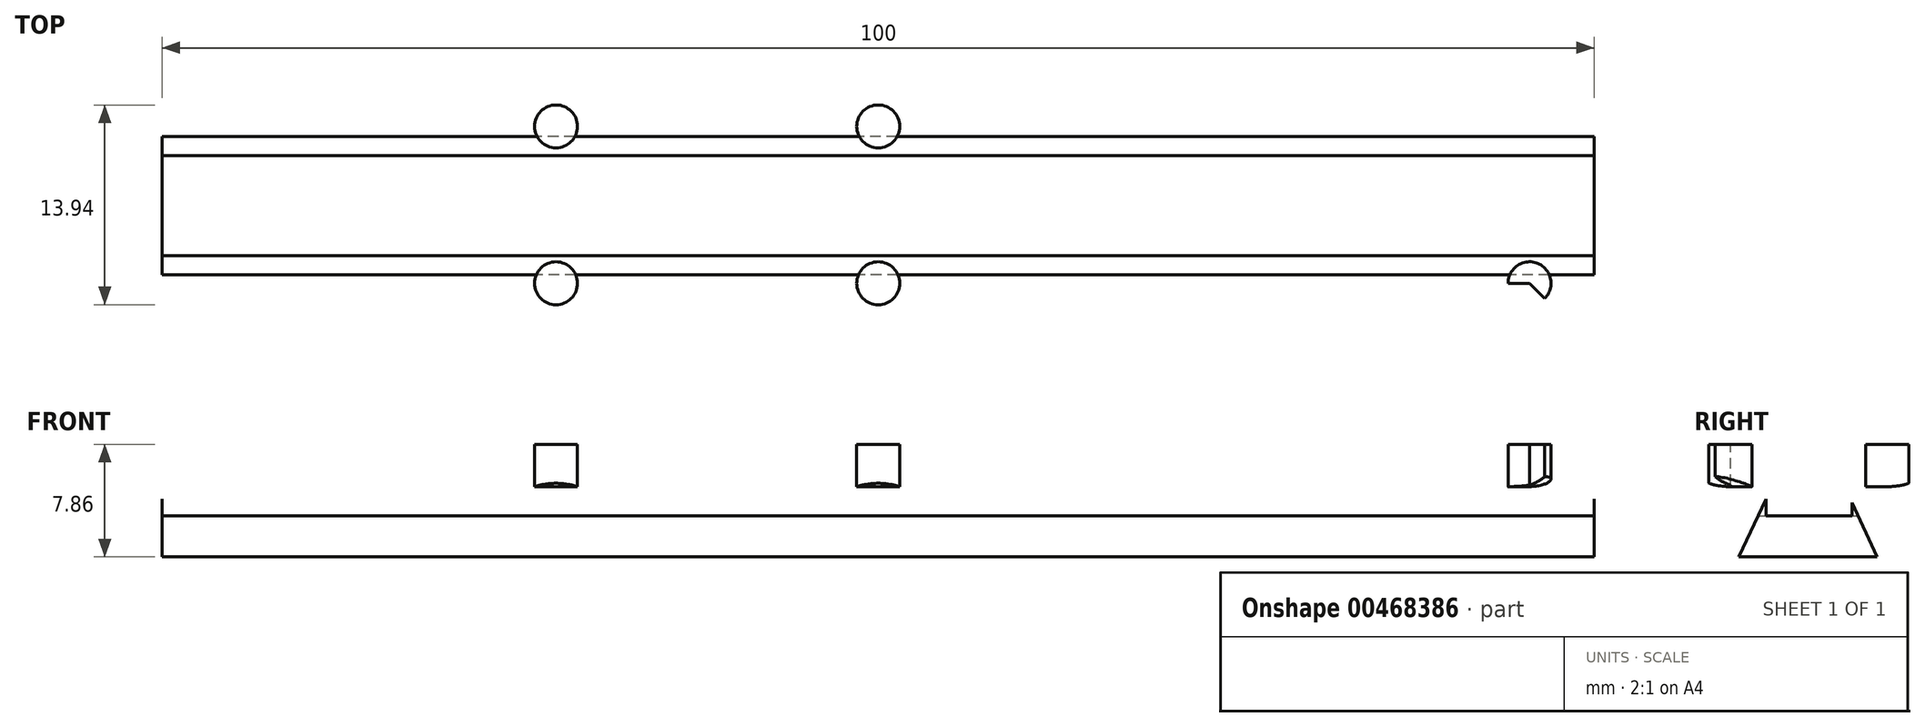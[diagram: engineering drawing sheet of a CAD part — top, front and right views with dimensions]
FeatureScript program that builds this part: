
annotation { "Feature Type Name" : "Feature", "Feature Type Description" : "" }
export const myFeature = defineFeature(function(context is Context, id is Id, definition is map)
    precondition{}
    {
        {
            var Q0;
            Q0=qCreatedBy(makeId("Right.planeOp"),FACE);
            var sketch = newSketch(context, id + "F0", { "sketchPlane" : qUnion([Q0])});
            skPoint(sketch, "E0", {"position": v(0, 0) * mm});
            skLineSegment(sketch, "E1", {"start": v(10, 0) * mm, "end": v(-10, 0) * mm});
            skPoint(sketch, "E2", {"position": v(0, -5) * mm});
            skLineSegment(sketch, "E3", {"start": v(10, -5) * mm, "end": v(-10, -5) * mm});
            skPoint(sketch, "E4", {"position": v(-2.6, 0) * mm});
            skPoint(sketch, "E5", {"position": v(2.6, 0) * mm});
            skLineSegment(sketch, "E6", {"start": v(-2.6, 0) * mm, "end": v(-4.93, -5) * mm});
            skLineSegment(sketch, "E7", {"start": v(2.6, 0) * mm, "end": v(4.93, -5) * mm});
            skLineSegment(sketch, "E8.0", {"start": v(10, -4.9) * mm, "end": v(-10.65, -4.9) * mm});
            skLineSegment(sketch, "E9.0", {"start": v(-2.7, 0.04) * mm, "end": v(-5.27, -5.49) * mm});
            skLineSegment(sketch, "E10.0", {"start": v(2.5, -0.04) * mm, "end": v(5.09, -5.57) * mm});
            skLineSegment(sketch, "E11.0", {"start": v(10, -0.1) * mm, "end": v(-10, -0.1) * mm});
            skLineSegment(sketch, "E12", {"start": v(-10, -0.1) * mm, "end": v(-10, 0) * mm});
            skLineSegment(sketch, "E13", {"start": v(10, -4.9) * mm, "end": v(10, -5) * mm});
            skLineSegment(sketch, "E14", {"start": v(10, 0) * mm, "end": v(10, -0.1) * mm});
            skLineSegment(sketch, "E15", {"start": v(-5.04, -5) * mm, "end": v(-5.27, -5.49) * mm});
            skLineSegment(sketch, "E16", {"start": v(2.5, -0.04) * mm, "end": v(2.49, 0) * mm});
            skLineSegment(sketch, "E17", {"start": v(10, 0) * mm, "end": v(10, 2.96) * mm});
            skLineSegment(sketch, "E18", {"start": v(10, 2.96) * mm, "end": v(-10, 2.96) * mm});
            skLineSegment(sketch, "E19", {"start": v(-10, 2.96) * mm, "end": v(-10, 0) * mm});
            skSolve(sketch);
        }
        {
            var Q0;
            {var subQ0=sQuery(id+"F0.wireOp",EDGE,"E11.0");var subQ1=sQuery(id+"F0.wireOp",EDGE,"E6");var subQ2=makeQuery(id+"F0.imprint","INTERSECT",VERTEX,{"derivedFrom":[subQ1,subQ0]});Q0=makeQuery(id+"F0.imprint","IMPRINT",FACE,{"disambiguationData":[TD([[makeQuery(id+"F0.imprint","IMPRINT",EDGE,{"disambiguationData":[TD([[subQ2,-1.0]])],"derivedFrom":subQ1}),1.0]])]});}
            var Q1;
            {var subQ7=sQuery(id+"F0.wireOp",EDGE,"E16");Q1=makeQuery(id+"F0.imprint","IMPRINT",FACE,{"disambiguationData":[TD([[makeQuery(id+"F0.imprint","IMPRINT",EDGE,{"derivedFrom":subQ7}),1.0]])]});}
            var Q2;
            {var subQ6=sQuery(id+"F0.wireOp",EDGE,"E17");Q2=makeQuery(id+"F0.imprint","IMPRINT",FACE,{"disambiguationData":[TD([[makeQuery(id+"F0.imprint","IMPRINT",EDGE,{"derivedFrom":subQ6}),1.0]])]});}
            extrude(context, id + "F1", {"entities" : qUnion([Q0, Q1, Q2]), "depth" : 100 * mm, "offsetDistance" : 25 * mm});
        }
        {
            var Q0;
            Q0=makeQuery(id+"F1.opExtrude","CAP_EDGE",EDGE,{"disambiguationData":[OSD([sQuery(id+"F0.wireOp",EDGE,"E19")])],"isStart":false});
            var Q1;
            Q1=makeQuery(id+"F1.opExtrude","CAP_EDGE",EDGE,{"disambiguationData":[OSD([sQuery(id+"F0.wireOp",EDGE,"E17")])],"isStart":false});
            var Q2;
            Q2=makeQuery(id+"F1.opExtrude","CAP_EDGE",EDGE,{"disambiguationData":[OSD([sQuery(id+"F0.wireOp",EDGE,"E19")])],"isStart":true});
            var Q3;
            Q3=makeQuery(id+"F1.opExtrude","CAP_EDGE",EDGE,{"disambiguationData":[OSD([sQuery(id+"F0.wireOp",EDGE,"E17")])],"isStart":true});
            fillet(context, id + "F2", {"entities" : qUnion([Q0, Q1, Q2, Q3]), "tangentPropagation" : true, "radius" : 7 * mm, "defaultsChanged" : true, "vertexSettings" : [], "allowEdgeOverflow" : false});
        }
        {
            var Q0;
            Q0=makeQuery(id+"F1.opExtrude","SWEPT_EDGE",EDGE,{"disambiguationData":[OSD([sQuery(id+"F0.wireOp",EDGE,"E1"),sQuery(id+"F0.wireOp",EDGE,"E12"),sQuery(id+"F0.wireOp",EDGE,"E19")])]});
            var Q1;
            Q1=makeQuery(id+"F1.opExtrude","SWEPT_EDGE",EDGE,{"disambiguationData":[OSD([sQuery(id+"F0.wireOp",EDGE,"E1"),sQuery(id+"F0.wireOp",EDGE,"E14"),sQuery(id+"F0.wireOp",EDGE,"E17")])]});
            fillet(context, id + "F3", {"entities" : qUnion([Q0, Q1]), "tangentPropagation" : true, "radius" : 5 * mm, "defaultsChanged" : false, "vertexSettings" : [], "allowEdgeOverflow" : false});
        }
        {
            var Q0;
            Q0=makeQuery(id+"F1.opExtrude","SWEPT_FACE",FACE,{"disambiguationData":[OSD([sQuery(id+"F0.wireOp",EDGE,"E18")])]});
            var sketch = newSketch(context, id + "F4", { "sketchPlane" : qUnion([Q0])});
            skArc(sketch, "E20.0", {"start": v(93, -10) * mm, "mid": v(97.95, -7.95) * mm, "end": v(100, -3) * mm});
            skArc(sketch, "E21.0", {"start": v(100, 3) * mm, "mid": v(97.95, 7.95) * mm, "end": v(93, 10) * mm});
            skArc(sketch, "E22.0", {"start": v(0, -3) * mm, "mid": v(2.05, -7.95) * mm, "end": v(7, -10) * mm});
            skArc(sketch, "E23.0", {"start": v(7, 10) * mm, "mid": v(2.05, 7.95) * mm, "end": v(0, 3) * mm});
            skLineSegment(sketch, "E24", {"start": v(7, -3) * mm, "end": v(2.05, -7.95) * mm});
            skLineSegment(sketch, "E25", {"start": v(7, 3) * mm, "end": v(2.05, 7.95) * mm});
            skLineSegment(sketch, "E26", {"start": v(93, -3) * mm, "end": v(97.95, -7.95) * mm});
            skLineSegment(sketch, "E27", {"start": v(93, 3) * mm, "end": v(97.95, 7.95) * mm});
            skCircle(sketch, "E28", {"center": v(95.47, 5.47) * mm, "radius": 1.5 * mm});
            skCircle(sketch, "E29", {"center": v(95.47, -5.47) * mm, "radius": 1.5 * mm});
            skCircle(sketch, "E30", {"center": v(4.53, -5.47) * mm, "radius": 1.5 * mm});
            skCircle(sketch, "E31", {"center": v(4.53, 5.47) * mm, "radius": 1.5 * mm});
            skLineSegment(sketch, "E32", {"start": v(95.47, -5.47) * mm, "end": v(4.53, -5.47) * mm});
            skLineSegment(sketch, "E33", {"start": v(95.47, 5.47) * mm, "end": v(4.53, 5.47) * mm});
            skCircle(sketch, "E34", {"center": v(50, 5.47) * mm, "radius": 1.5 * mm});
            skCircle(sketch, "E35", {"center": v(50, -5.47) * mm, "radius": 1.5 * mm});
            skPoint(sketch, "E36", {"position": v(27.5, -5.47) * mm});
            skPoint(sketch, "E37", {"position": v(27.5, 5.47) * mm});
            skPoint(sketch, "E38", {"position": v(72.5, -5.47) * mm});
            skPoint(sketch, "E39", {"position": v(72.5, 5.47) * mm});
            skCircle(sketch, "E40", {"center": v(27.5, 5.47) * mm, "radius": 1.5 * mm});
            skCircle(sketch, "E41", {"center": v(27.5, -5.47) * mm, "radius": 1.5 * mm});
            skCircle(sketch, "E42", {"center": v(72.5, 5.47) * mm, "radius": 1.5 * mm});
            skCircle(sketch, "E43", {"center": v(72.5, -5.47) * mm, "radius": 1.5 * mm});
            skSolve(sketch);
        }
        {
            var Q0;
            {var subQ0=sQuery(id+"F4.wireOp",EDGE,"E28");var subQ1=sQuery(id+"F4.wireOp",EDGE,"E27");var subQ2=makeQuery(id+"F4.imprint","INTERSECT",VERTEX,{"disambiguationData":[OD(0.0)],"derivedFrom":[subQ1,subQ0]});Q0=makeQuery(id+"F4.imprint","IMPRINT",FACE,{"disambiguationData":[TD([[makeQuery(id+"F4.imprint","IMPRINT",EDGE,{"disambiguationData":[TD([[subQ2,-1.0]])],"derivedFrom":subQ1}),-1.0]])]});}
            var Q1;
            {var subQ0=sQuery(id+"F4.wireOp",EDGE,"E28");var subQ1=sQuery(id+"F4.wireOp",EDGE,"E27");var subQ2=makeQuery(id+"F4.imprint","INTERSECT",VERTEX,{"disambiguationData":[OD(0.0)],"derivedFrom":[subQ1,subQ0]});Q1=makeQuery(id+"F4.imprint","IMPRINT",FACE,{"disambiguationData":[TD([[makeQuery(id+"F4.imprint","IMPRINT",EDGE,{"disambiguationData":[TD([[subQ2,-1.0]])],"derivedFrom":subQ1}),1.0]])]});}
            var Q2;
            {var subQ0=sQuery(id+"F4.wireOp",EDGE,"E29");var subQ1=sQuery(id+"F4.wireOp",EDGE,"E26");var subQ2=makeQuery(id+"F4.imprint","INTERSECT",VERTEX,{"disambiguationData":[OD(0.0)],"derivedFrom":[subQ1,subQ0]});Q2=makeQuery(id+"F4.imprint","IMPRINT",FACE,{"disambiguationData":[TD([[makeQuery(id+"F4.imprint","IMPRINT",EDGE,{"disambiguationData":[TD([[subQ2,-1.0]])],"derivedFrom":subQ1}),1.0]])]});}
            var Q3;
            {var subQ0=sQuery(id+"F4.wireOp",EDGE,"E29");var subQ1=sQuery(id+"F4.wireOp",EDGE,"E26");var subQ2=makeQuery(id+"F4.imprint","INTERSECT",VERTEX,{"disambiguationData":[OD(0.0)],"derivedFrom":[subQ1,subQ0]});Q3=makeQuery(id+"F4.imprint","IMPRINT",FACE,{"disambiguationData":[TD([[makeQuery(id+"F4.imprint","IMPRINT",EDGE,{"disambiguationData":[TD([[subQ2,-1.0]])],"derivedFrom":subQ1}),-1.0]])]});}
            var Q4;
            {var subQ0=sQuery(id+"F4.wireOp",EDGE,"E32");var subQ1=sQuery(id+"F4.wireOp",EDGE,"E26");var subQ2=makeQuery(id+"F4.imprint","INTERSECT",VERTEX,{"derivedFrom":[subQ1,subQ0]});Q4=makeQuery(id+"F4.imprint","IMPRINT",FACE,{"disambiguationData":[TD([[makeQuery(id+"F4.imprint","IMPRINT",EDGE,{"disambiguationData":[TD([[subQ2,-1.0]])],"derivedFrom":subQ1}),-1.0]])]});}
            var Q5;
            {var subQ0=sQuery(id+"F4.wireOp",EDGE,"E33");var subQ1=sQuery(id+"F4.wireOp",EDGE,"E27");var subQ2=makeQuery(id+"F4.imprint","INTERSECT",VERTEX,{"derivedFrom":[subQ1,subQ0]});Q5=makeQuery(id+"F4.imprint","IMPRINT",FACE,{"disambiguationData":[TD([[makeQuery(id+"F4.imprint","IMPRINT",EDGE,{"disambiguationData":[TD([[subQ2,-1.0]])],"derivedFrom":subQ1}),1.0]])]});}
            var Q6;
            {var subQ0=sQuery(id+"F4.wireOp",EDGE,"E43");var subQ1=sQuery(id+"F4.wireOp",EDGE,"E32");var subQ2=makeQuery(id+"F4.imprint","INTERSECT",VERTEX,{"disambiguationData":[OD(0.0)],"derivedFrom":[subQ1,subQ0]});Q6=makeQuery(id+"F4.imprint","IMPRINT",FACE,{"disambiguationData":[TD([[makeQuery(id+"F4.imprint","IMPRINT",EDGE,{"disambiguationData":[TD([[subQ2,-1.0]])],"derivedFrom":subQ1}),1.0]])]});}
            var Q7;
            {var subQ0=sQuery(id+"F4.wireOp",EDGE,"E43");var subQ1=sQuery(id+"F4.wireOp",EDGE,"E32");var subQ2=makeQuery(id+"F4.imprint","INTERSECT",VERTEX,{"disambiguationData":[OD(0.0)],"derivedFrom":[subQ1,subQ0]});Q7=makeQuery(id+"F4.imprint","IMPRINT",FACE,{"disambiguationData":[TD([[makeQuery(id+"F4.imprint","IMPRINT",EDGE,{"disambiguationData":[TD([[subQ2,-1.0]])],"derivedFrom":subQ1}),-1.0]])]});}
            var Q8;
            {var subQ0=sQuery(id+"F4.wireOp",EDGE,"E42");var subQ1=sQuery(id+"F4.wireOp",EDGE,"E33");var subQ2=makeQuery(id+"F4.imprint","INTERSECT",VERTEX,{"disambiguationData":[OD(0.0)],"derivedFrom":[subQ1,subQ0]});Q8=makeQuery(id+"F4.imprint","IMPRINT",FACE,{"disambiguationData":[TD([[makeQuery(id+"F4.imprint","IMPRINT",EDGE,{"disambiguationData":[TD([[subQ2,-1.0]])],"derivedFrom":subQ1}),1.0]])]});}
            var Q9;
            {var subQ0=sQuery(id+"F4.wireOp",EDGE,"E42");var subQ1=sQuery(id+"F4.wireOp",EDGE,"E33");var subQ2=makeQuery(id+"F4.imprint","INTERSECT",VERTEX,{"disambiguationData":[OD(0.0)],"derivedFrom":[subQ1,subQ0]});Q9=makeQuery(id+"F4.imprint","IMPRINT",FACE,{"disambiguationData":[TD([[makeQuery(id+"F4.imprint","IMPRINT",EDGE,{"disambiguationData":[TD([[subQ2,-1.0]])],"derivedFrom":subQ1}),-1.0]])]});}
            var Q10;
            {var subQ0=sQuery(id+"F4.wireOp",EDGE,"E35");var subQ1=sQuery(id+"F4.wireOp",EDGE,"E32");var subQ2=makeQuery(id+"F4.imprint","INTERSECT",VERTEX,{"disambiguationData":[OD(0.0)],"derivedFrom":[subQ1,subQ0]});Q10=makeQuery(id+"F4.imprint","IMPRINT",FACE,{"disambiguationData":[TD([[makeQuery(id+"F4.imprint","IMPRINT",EDGE,{"disambiguationData":[TD([[subQ2,-1.0]])],"derivedFrom":subQ1}),1.0]])]});}
            var Q11;
            {var subQ0=sQuery(id+"F4.wireOp",EDGE,"E35");var subQ1=sQuery(id+"F4.wireOp",EDGE,"E32");var subQ2=makeQuery(id+"F4.imprint","INTERSECT",VERTEX,{"disambiguationData":[OD(0.0)],"derivedFrom":[subQ1,subQ0]});Q11=makeQuery(id+"F4.imprint","IMPRINT",FACE,{"disambiguationData":[TD([[makeQuery(id+"F4.imprint","IMPRINT",EDGE,{"disambiguationData":[TD([[subQ2,-1.0]])],"derivedFrom":subQ1}),-1.0]])]});}
            var Q12;
            {var subQ0=sQuery(id+"F4.wireOp",EDGE,"E34");var subQ1=sQuery(id+"F4.wireOp",EDGE,"E33");var subQ2=makeQuery(id+"F4.imprint","INTERSECT",VERTEX,{"disambiguationData":[OD(0.0)],"derivedFrom":[subQ1,subQ0]});Q12=makeQuery(id+"F4.imprint","IMPRINT",FACE,{"disambiguationData":[TD([[makeQuery(id+"F4.imprint","IMPRINT",EDGE,{"disambiguationData":[TD([[subQ2,-1.0]])],"derivedFrom":subQ1}),1.0]])]});}
            var Q13;
            {var subQ0=sQuery(id+"F4.wireOp",EDGE,"E34");var subQ1=sQuery(id+"F4.wireOp",EDGE,"E33");var subQ2=makeQuery(id+"F4.imprint","INTERSECT",VERTEX,{"disambiguationData":[OD(0.0)],"derivedFrom":[subQ1,subQ0]});Q13=makeQuery(id+"F4.imprint","IMPRINT",FACE,{"disambiguationData":[TD([[makeQuery(id+"F4.imprint","IMPRINT",EDGE,{"disambiguationData":[TD([[subQ2,-1.0]])],"derivedFrom":subQ1}),-1.0]])]});}
            var Q14;
            {var subQ0=sQuery(id+"F4.wireOp",EDGE,"E41");var subQ1=sQuery(id+"F4.wireOp",EDGE,"E32");var subQ2=makeQuery(id+"F4.imprint","INTERSECT",VERTEX,{"disambiguationData":[OD(0.0)],"derivedFrom":[subQ1,subQ0]});Q14=makeQuery(id+"F4.imprint","IMPRINT",FACE,{"disambiguationData":[TD([[makeQuery(id+"F4.imprint","IMPRINT",EDGE,{"disambiguationData":[TD([[subQ2,-1.0]])],"derivedFrom":subQ1}),1.0]])]});}
            var Q15;
            {var subQ0=sQuery(id+"F4.wireOp",EDGE,"E41");var subQ1=sQuery(id+"F4.wireOp",EDGE,"E32");var subQ2=makeQuery(id+"F4.imprint","INTERSECT",VERTEX,{"disambiguationData":[OD(0.0)],"derivedFrom":[subQ1,subQ0]});Q15=makeQuery(id+"F4.imprint","IMPRINT",FACE,{"disambiguationData":[TD([[makeQuery(id+"F4.imprint","IMPRINT",EDGE,{"disambiguationData":[TD([[subQ2,-1.0]])],"derivedFrom":subQ1}),-1.0]])]});}
            var Q16;
            {var subQ0=sQuery(id+"F4.wireOp",EDGE,"E40");var subQ1=sQuery(id+"F4.wireOp",EDGE,"E33");var subQ2=makeQuery(id+"F4.imprint","INTERSECT",VERTEX,{"disambiguationData":[OD(0.0)],"derivedFrom":[subQ1,subQ0]});Q16=makeQuery(id+"F4.imprint","IMPRINT",FACE,{"disambiguationData":[TD([[makeQuery(id+"F4.imprint","IMPRINT",EDGE,{"disambiguationData":[TD([[subQ2,-1.0]])],"derivedFrom":subQ1}),1.0]])]});}
            var Q17;
            {var subQ0=sQuery(id+"F4.wireOp",EDGE,"E40");var subQ1=sQuery(id+"F4.wireOp",EDGE,"E33");var subQ2=makeQuery(id+"F4.imprint","INTERSECT",VERTEX,{"disambiguationData":[OD(0.0)],"derivedFrom":[subQ1,subQ0]});Q17=makeQuery(id+"F4.imprint","IMPRINT",FACE,{"disambiguationData":[TD([[makeQuery(id+"F4.imprint","IMPRINT",EDGE,{"disambiguationData":[TD([[subQ2,-1.0]])],"derivedFrom":subQ1}),-1.0]])]});}
            var Q18;
            {var subQ0=sQuery(id+"F4.wireOp",EDGE,"E32");var subQ1=sQuery(id+"F4.wireOp",EDGE,"E24");var subQ2=makeQuery(id+"F4.imprint","INTERSECT",VERTEX,{"derivedFrom":[subQ1,subQ0]});Q18=makeQuery(id+"F4.imprint","IMPRINT",FACE,{"disambiguationData":[TD([[makeQuery(id+"F4.imprint","IMPRINT",EDGE,{"disambiguationData":[TD([[subQ2,-1.0]])],"derivedFrom":subQ1}),1.0]])]});}
            var Q19;
            {var subQ0=sQuery(id+"F4.wireOp",EDGE,"E24");var subQ1=makeQuery(id+"F4.imprint","INTERSECT",VERTEX,{"derivedFrom":[subQ0,sQuery(id+"F4.wireOp",EDGE,"E32")]});Q19=makeQuery(id+"F4.imprint","IMPRINT",FACE,{"disambiguationData":[TD([[makeQuery(id+"F4.imprint","IMPRINT",EDGE,{"disambiguationData":[TD([[subQ1,1.0]])],"derivedFrom":subQ0}),-1.0]])]});}
            var Q20;
            {var subQ0=sQuery(id+"F4.wireOp",EDGE,"E32");var subQ1=sQuery(id+"F4.wireOp",EDGE,"E24");var subQ2=makeQuery(id+"F4.imprint","INTERSECT",VERTEX,{"derivedFrom":[subQ1,subQ0]});Q20=makeQuery(id+"F4.imprint","IMPRINT",FACE,{"disambiguationData":[TD([[makeQuery(id+"F4.imprint","IMPRINT",EDGE,{"disambiguationData":[TD([[subQ2,1.0]])],"derivedFrom":subQ1}),1.0]])]});}
            var Q21;
            {var subQ0=sQuery(id+"F4.wireOp",EDGE,"E33");var subQ1=sQuery(id+"F4.wireOp",EDGE,"E25");var subQ2=makeQuery(id+"F4.imprint","INTERSECT",VERTEX,{"derivedFrom":[subQ1,subQ0]});Q21=makeQuery(id+"F4.imprint","IMPRINT",FACE,{"disambiguationData":[TD([[makeQuery(id+"F4.imprint","IMPRINT",EDGE,{"disambiguationData":[TD([[subQ2,1.0]])],"derivedFrom":subQ1}),-1.0]])]});}
            var Q22;
            {var subQ0=sQuery(id+"F4.wireOp",EDGE,"E25");var subQ1=makeQuery(id+"F4.imprint","INTERSECT",VERTEX,{"derivedFrom":[subQ0,sQuery(id+"F4.wireOp",EDGE,"E33")]});Q22=makeQuery(id+"F4.imprint","IMPRINT",FACE,{"disambiguationData":[TD([[makeQuery(id+"F4.imprint","IMPRINT",EDGE,{"disambiguationData":[TD([[subQ1,1.0]])],"derivedFrom":subQ0}),1.0]])]});}
            var Q23;
            {var subQ0=sQuery(id+"F4.wireOp",EDGE,"E33");var subQ1=sQuery(id+"F4.wireOp",EDGE,"E25");var subQ2=makeQuery(id+"F4.imprint","INTERSECT",VERTEX,{"derivedFrom":[subQ1,subQ0]});Q23=makeQuery(id+"F4.imprint","IMPRINT",FACE,{"disambiguationData":[TD([[makeQuery(id+"F4.imprint","IMPRINT",EDGE,{"disambiguationData":[TD([[subQ2,-1.0]])],"derivedFrom":subQ1}),-1.0]])]});}
            extrude(context, id + "F5", {"entities" : qUnion([Q0, Q1, Q2, Q3, Q4, Q5, Q6, Q7, Q8, Q9, Q10, Q11, Q12, Q13, Q14, Q15, Q16, Q17, Q18, Q19, Q20, Q21, Q22, Q23]), "operationType" : NewBodyOperationType.REMOVE, "oppositeDirection" : true, "depth" : 5 * mm, "offsetDistance" : 25 * mm});
        }
    });
